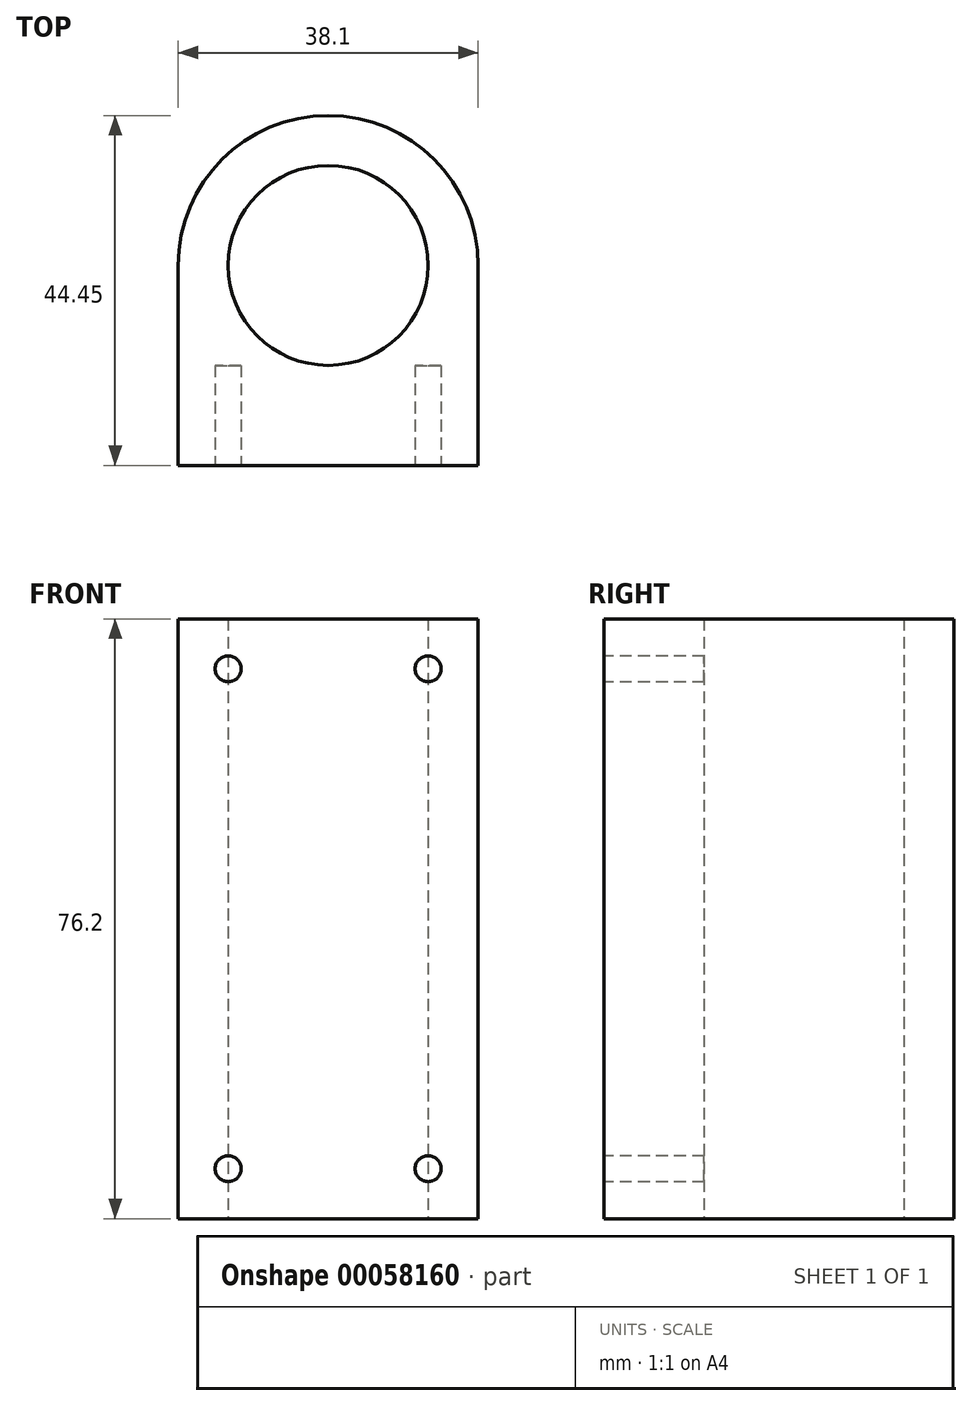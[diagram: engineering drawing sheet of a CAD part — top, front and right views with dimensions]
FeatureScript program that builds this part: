
annotation { "Feature Type Name" : "Feature", "Feature Type Description" : "" }
export const myFeature = defineFeature(function(context is Context, id is Id, definition is map)
    precondition{}
    {
        {
            var Q0;
            Q0=qCreatedBy(makeId("Top.planeOp"),FACE);
            var sketch = newSketch(context, id + "F0", { "sketchPlane" : qUnion([Q0])});
            skCircle(sketch, "E0", {"center": v(0, 0) * mm, "radius": 12.7 * mm});
            skArc(sketch, "E1", {"start": v(19.05, 0) * mm, "mid": v(0, 19.05) * mm, "end": v(-19.05, 0) * mm});
            skLineSegment(sketch, "E2", {"start": v(-19.05, 0) * mm, "end": v(-19.05, -25.4) * mm});
            skLineSegment(sketch, "E3", {"start": v(-19.05, -25.4) * mm, "end": v(19.05, -25.4) * mm});
            skLineSegment(sketch, "E4", {"start": v(19.05, -25.4) * mm, "end": v(19.05, 0) * mm});
            skSolve(sketch);
        }
        {
            var Q0;
            Q0=makeQuery(id+"F0.imprint","IMPRINT",FACE,{"disambiguationData":[TD([[makeQuery(id+"F0.imprint","IMPRINT",EDGE,{"derivedFrom":sQuery(id+"F0.wireOp",EDGE,"E0")}),-1.0]])]});
            extrude(context, id + "F1", {"entities" : qUnion([Q0]), "depth" : 76.2 * mm});
        }
        {
            var Q0;
            Q0=makeQuery(id+"F1.opExtrude","SWEPT_FACE",FACE,{"disambiguationData":[OSD([sQuery(id+"F0.wireOp",EDGE,"E3")])]});
            var sketch = newSketch(context, id + "F2", { "sketchPlane" : qUnion([Q0])});
            skCircle(sketch, "E5", {"center": v(12.7, 6.35) * mm, "radius": 1.65 * mm});
            skCircle(sketch, "E6", {"center": v(12.7, 69.85) * mm, "radius": 1.65 * mm});
            skCircle(sketch, "E7", {"center": v(-12.7, 69.85) * mm, "radius": 1.65 * mm});
            skCircle(sketch, "E8", {"center": v(-12.7, 6.35) * mm, "radius": 1.65 * mm});
            skSolve(sketch);
        }
        {
            var Q0;
            Q0=makeQuery(id+"F2.imprint","IMPRINT",FACE,{"disambiguationData":[TD([[makeQuery(id+"F2.imprint","IMPRINT",EDGE,{"derivedFrom":sQuery(id+"F2.wireOp",EDGE,"E5")}),1.0]])]});
            var Q1;
            Q1=makeQuery(id+"F2.imprint","IMPRINT",FACE,{"disambiguationData":[TD([[makeQuery(id+"F2.imprint","IMPRINT",EDGE,{"derivedFrom":sQuery(id+"F2.wireOp",EDGE,"E8")}),1.0]])]});
            var Q2;
            Q2=makeQuery(id+"F2.imprint","IMPRINT",FACE,{"disambiguationData":[TD([[makeQuery(id+"F2.imprint","IMPRINT",EDGE,{"derivedFrom":sQuery(id+"F2.wireOp",EDGE,"E7")}),1.0]])]});
            var Q3;
            Q3=makeQuery(id+"F2.imprint","IMPRINT",FACE,{"disambiguationData":[TD([[makeQuery(id+"F2.imprint","IMPRINT",EDGE,{"derivedFrom":sQuery(id+"F2.wireOp",EDGE,"E6")}),1.0]])]});
            extrude(context, id + "F3", {"entities" : qUnion([Q0, Q1, Q2, Q3]), "operationType" : NewBodyOperationType.REMOVE, "oppositeDirection" : true, "depth" : 12.7 * mm});
        }
    });
